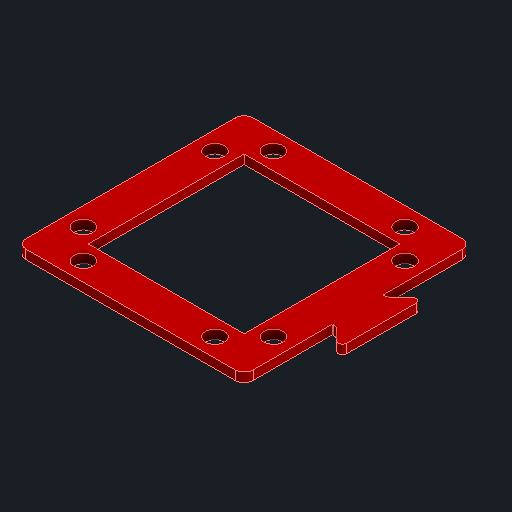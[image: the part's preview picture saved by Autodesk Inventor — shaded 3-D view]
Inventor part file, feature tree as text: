
AUTODESK INVENTOR PART (.ipt)
format: ipt  version: 2023.4 (Build 274418000, 418)  size: 364,544 bytes
history: native  units: mm
features: reference x9, extrude x3, other x3, sketch x2, fillet x1, projected_geometry x1
ambient origin geometry x8: Origin, YZ Plane, XZ Plane, XY Plane, X Axis, Y Axis, Z Axis, Center Point
bodies: Solid1 (feature_tree)
feature tree (19):
  extrude  "Extrusion1"  Depth=2.0mm TaperAngle=0.0deg
  sketch  "Sketch2"  dims[d16=10.0mm d17=0.0mm d18=0.25mm d19=20.0mm d20=10.0mm d21=45.0deg d22=1.0mm d23=1.5mm d24=1.0mm d25=0.075mm d28=15.171573mm d29=2.87868mm d30=2.87868mm d31=20.0mm d32=10.0mm d33=45.0deg d34=1.0mm d35=1.5mm d36=1.0mm d37=0.075mm d38=15.171573mm d39=2.87868mm d40=2.87868mm d41=0.25mm d42=0.0mm d43=40.0mm d45=360.0deg]
  extrude  "Extrusion2"  Depth=10.0mm
  extrude  "Extrusion3"  Depth=10.0mm
  fillet  "Fillet1"  Radius=2.87868mm
  sketch  "Sketch1"  dims[d0=2.0mm d1=0.0mm d14=2.0mm d15=0.0mm]
  reference  "Reference1"
  reference  "Reference2"
  reference  "Reference3"
  reference  "Reference4"
  reference  "Reference5"
  reference  "Reference6"
  reference  "Reference7"
  reference  "Reference8"
  reference  "Reference9"
  projected_geometry  "Projected Loop2"
  other  "<path>\Projects\Project Protocube\Protocube\CAD, STL, OBJ Files\1 CAD\Cube 1x1 V5.iam"
  other  "Cube 1x1 V5.iam"
  other  "Cube 1x1 Top V5:1"
note: 1 file-system path scrubbed to <path> (originals preserved in map.json)
